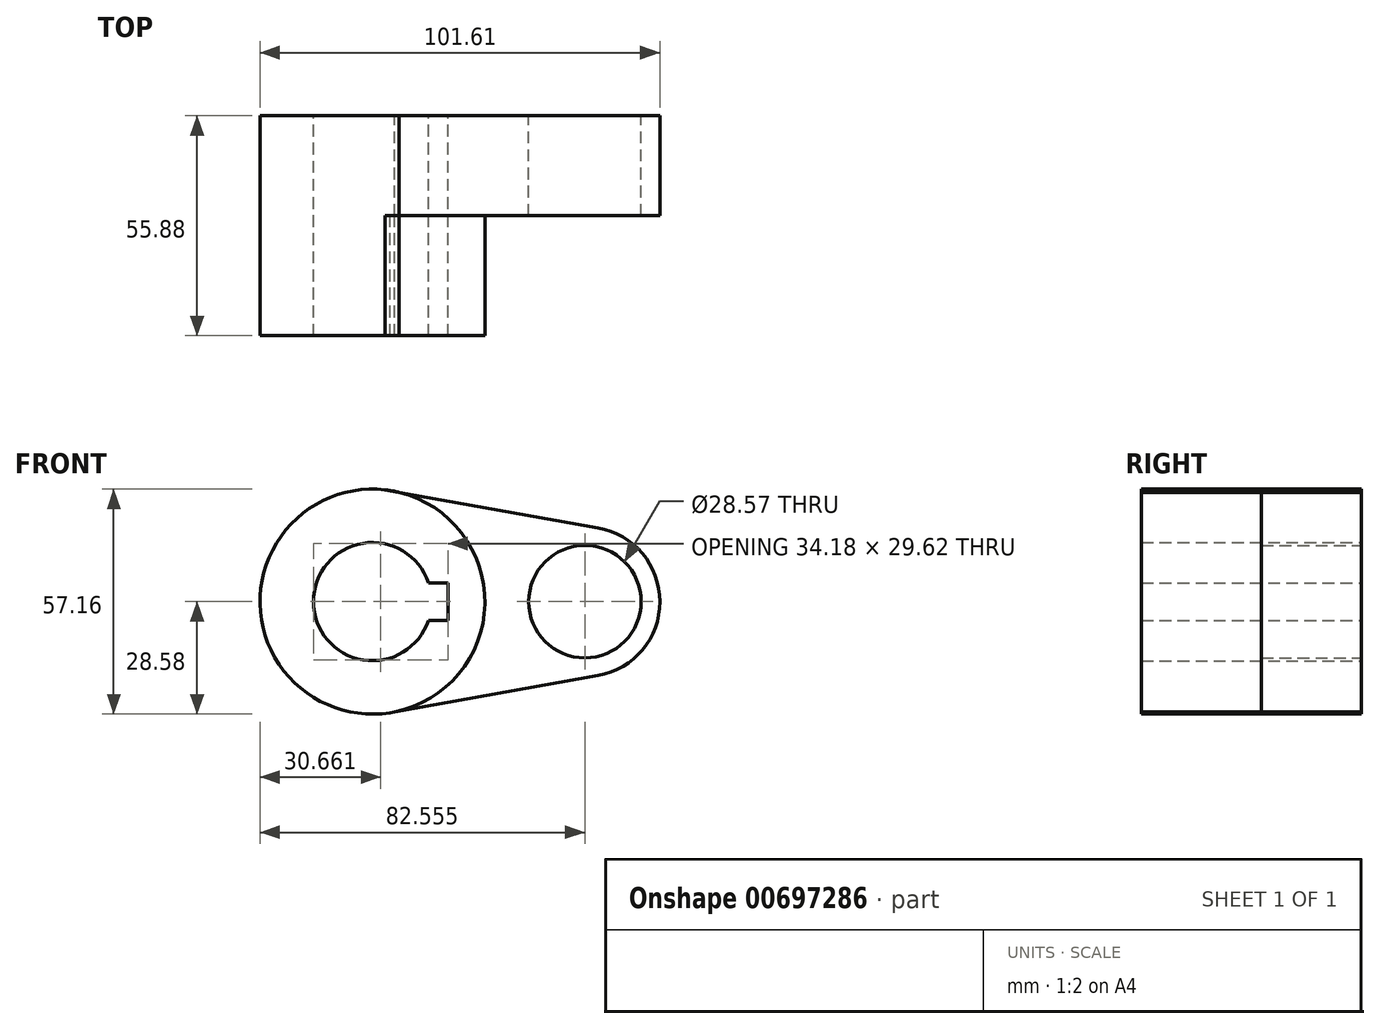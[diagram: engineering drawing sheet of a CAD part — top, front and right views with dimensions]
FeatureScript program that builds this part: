
annotation { "Feature Type Name" : "Feature", "Feature Type Description" : "" }
export const myFeature = defineFeature(function(context is Context, id is Id, definition is map)
    precondition{}
    {
        {
            var Q0;
            Q0=qCreatedBy(makeId("Front.planeOp"),FACE);
            var sketch = newSketch(context, id + "F0", { "sketchPlane" : qUnion([Q0])});
            skCircle(sketch, "E0", {"center": v(0, 0) * mm, "radius": 28.58 * mm});
            skCircle(sketch, "E1", {"center": v(53.98, 0) * mm, "radius": 19.05 * mm});
            skLineSegment(sketch, "E2", {"start": v(3.2, 28.4) * mm, "end": v(57.3, 18.76) * mm});
            skLineSegment(sketch, "E3", {"start": v(4.45, -28.23) * mm, "end": v(57.33, -18.75) * mm});
            skCircle(sketch, "E4", {"center": v(0, 0) * mm, "radius": 15 * mm});
            skCircle(sketch, "E5", {"center": v(53.98, 0) * mm, "radius": 14.29 * mm});
            skLineSegment(sketch, "E6.bottom", {"start": v(-19.17, 4.76) * mm, "end": v(19.17, 4.76) * mm});
            skLineSegment(sketch, "E6.top", {"start": v(-19.17, -4.76) * mm, "end": v(19.17, -4.76) * mm});
            skLineSegment(sketch, "E6.left", {"start": v(-19.17, 4.76) * mm, "end": v(-19.17, -4.76) * mm});
            skLineSegment(sketch, "E6.right", {"start": v(19.17, 4.76) * mm, "end": v(19.17, -4.76) * mm});
            skSolve(sketch);
        }
        {
            var Q0;
            Q0 = qSketchRegion(id + "F0", true);
            var Q1;
            {var subQ5=sQuery(id+"F0.wireOp",EDGE,"E6.left");Q1=makeQuery(id+"F0.imprint","IMPRINT",FACE,{"disambiguationData":[TD([[makeQuery(id+"F0.imprint","IMPRINT",EDGE,{"derivedFrom":subQ5}),1.0]])]});}
            extrude(context, id + "F1", {"entities" : qUnion([Q0, Q1]), "depth" : 25.4 * mm, "offsetDistance" : 25.4 * mm});
        }
        {
            var Q0;
            {var subQ4=sQuery(id+"F0.wireOp",EDGE,"E6.left");Q0=makeQuery(id+"F0.imprint","IMPRINT",FACE,{"disambiguationData":[TD([[makeQuery(id+"F0.imprint","IMPRINT",EDGE,{"derivedFrom":subQ4}),-1.0]])]});}
            var Q1;
            {var subQ5=sQuery(id+"F0.wireOp",EDGE,"E6.left");Q1=makeQuery(id+"F0.imprint","IMPRINT",FACE,{"disambiguationData":[TD([[makeQuery(id+"F0.imprint","IMPRINT",EDGE,{"derivedFrom":subQ5}),1.0]])]});}
            extrude(context, id + "F2", {"entities" : qUnion([Q0, Q1]), "operationType" : NewBodyOperationType.ADD, "depth" : 55.88 * mm, "offsetDistance" : 25.4 * mm});
        }
    });
